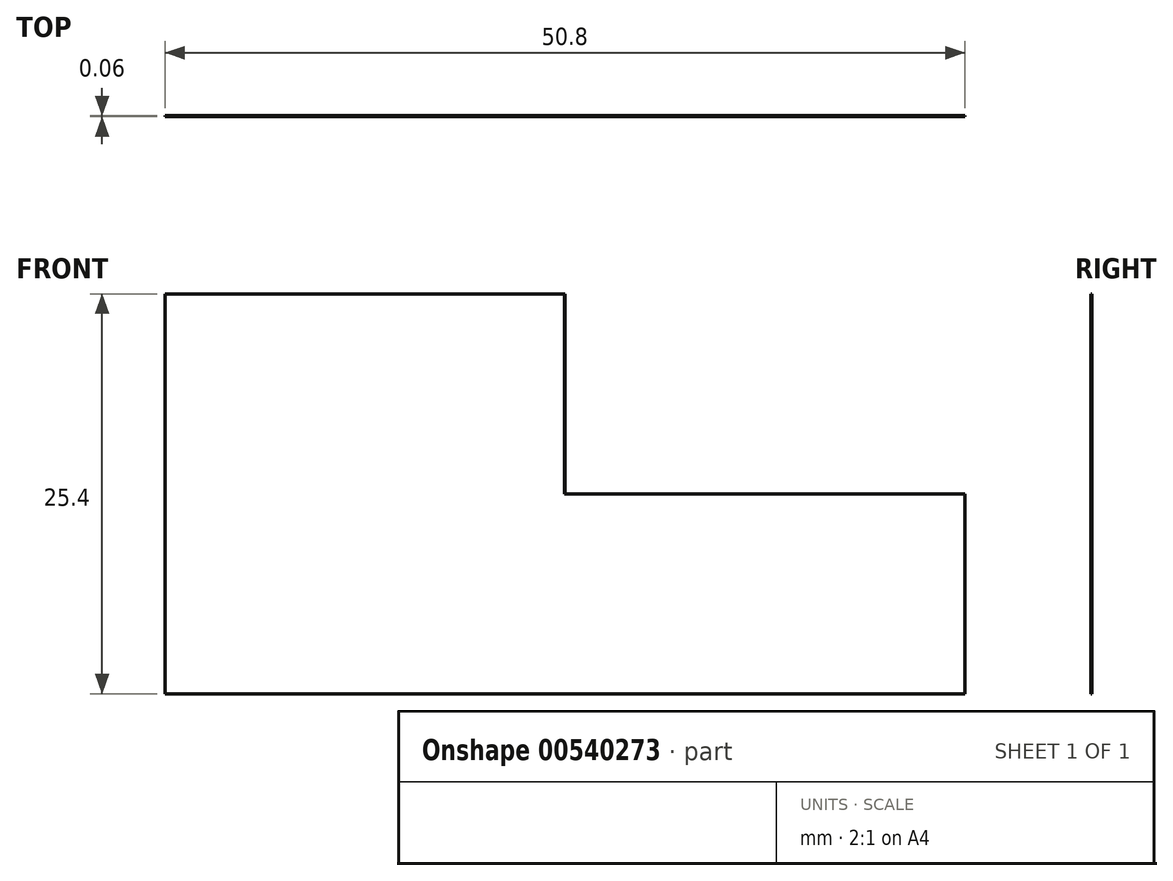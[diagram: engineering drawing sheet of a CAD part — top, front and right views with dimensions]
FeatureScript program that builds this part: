
annotation { "Feature Type Name" : "Feature", "Feature Type Description" : "" }
export const myFeature = defineFeature(function(context is Context, id is Id, definition is map)
    precondition{}
    {
        {
            var Q0;
            Q0=qCreatedBy(makeId("Front.planeOp"),FACE);
            var sketch = newSketch(context, id + "F0", { "sketchPlane" : qUnion([Q0])});
            skLineSegment(sketch, "E0", {"start": v(-66.16, 25.4) * mm, "end": v(-15.36, 25.4) * mm});
            skLineSegment(sketch, "E1", {"start": v(-15.36, 25.4) * mm, "end": v(-15.36, 0) * mm});
            skLineSegment(sketch, "E2", {"start": v(-15.36, 0) * mm, "end": v(-66.16, 0) * mm});
            skLineSegment(sketch, "E3", {"start": v(-66.16, 0) * mm, "end": v(-66.16, 25.4) * mm});
            skSolve(sketch);
        }
        {
            var Q0;
            Q0 = qSketchRegion(id + "F0", true);
            extrude(context, id + "F1", {"entities" : qUnion([Q0]), "depth" : 6 / 101.6 * mm, "offsetDistance" : 25.4 * mm});
        }
        {
            var Q0;
            Q0=makeQuery(id+"F1.opExtrude","SWEPT_FACE",FACE,{"disambiguationData":[OSD([sQuery(id+"F0.wireOp",EDGE,"E0")])]});
            var sketch = newSketch(context, id + "F2", { "sketchPlane" : qUnion([Q0])});
            skLineSegment(sketch, "E4", {"start": v(-40.76, 0) * mm, "end": v(-59.81, -38.1) * mm});
            skLineSegment(sketch, "E5", {"start": v(-15.36, -19.05) * mm, "end": v(-28.06, -38.1) * mm});
            skSolve(sketch);
        }
        {
            var Q0;
            {var subQ5=sQuery(id+"F2.wireOp",EDGE,"E4");Q0=makeQuery(id+"F2.imprint","IMPRINT",FACE,{"disambiguationData":[TD([[makeQuery(id+"F2.imprint","IMPRINT",EDGE,{"derivedFrom":subQ5}),1.0]])]});}
            extrude(context, id + "F3", {"entities" : qUnion([Q0]), "operationType" : NewBodyOperationType.REMOVE, "oppositeDirection" : true, "depth" : 12.7 * mm, "offsetDistance" : 25.4 * mm});
        }
    });
